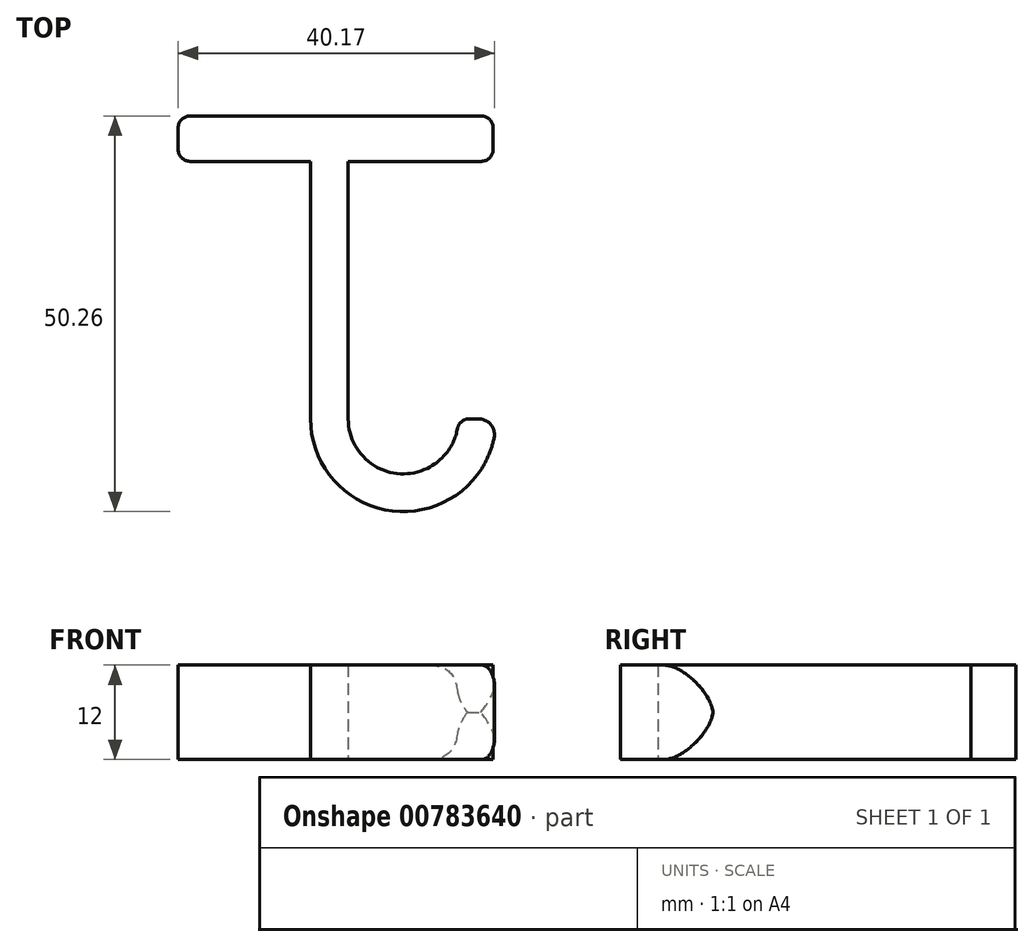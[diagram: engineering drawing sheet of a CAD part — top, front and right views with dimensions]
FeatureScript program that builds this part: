
annotation { "Feature Type Name" : "Feature", "Feature Type Description" : "" }
export const myFeature = defineFeature(function(context is Context, id is Id, definition is map)
    precondition{}
    {
        {
            var Q0;
            Q0=qCreatedBy(makeId("Top.planeOp"),FACE);
            var sketch = newSketch(context, id + "F0", { "sketchPlane" : qUnion([Q0])});
            skLineSegment(sketch, "E0.bottom", {"start": v(-44.99, 50) * mm, "end": v(-7.99, 50) * mm});
            skLineSegment(sketch, "E0.top", {"start": v(-44.99, 44.24) * mm, "end": v(-29.68, 44.24) * mm});
            skLineSegment(sketch, "E0.left", {"start": v(-46.49, 48.5) * mm, "end": v(-46.49, 45.74) * mm});
            skLineSegment(sketch, "E0.right", {"start": v(-6.49, 48.5) * mm, "end": v(-6.49, 45.74) * mm});
            skLineSegment(sketch, "E1.bottom", {"start": v(-29.68, 11.52) * mm, "end": v(-24.89, 11.52) * mm});
            skLineSegment(sketch, "E1.top", {"start": v(-29.68, 82.72) * mm, "end": v(-24.89, 82.72) * mm});
            skLineSegment(sketch, "E1.left", {"start": v(-29.68, 11.52) * mm, "end": v(-29.68, 50) * mm});
            skLineSegment(sketch, "E1.right", {"start": v(-24.89, 11.52) * mm, "end": v(-24.89, 44.24) * mm});
            skArc(sketch, "E2", {"start": v(-29.68, 11.52) * mm, "mid": v(-19.1, -0.2) * mm, "end": v(-6.36, 9.11) * mm});
            skArc(sketch, "E3", {"start": v(-24.89, 11.52) * mm, "mid": v(-18.52, 4.56) * mm, "end": v(-11.02, 10.28) * mm});
            skLineSegment(sketch, "E4", {"start": v(-8.32, 11.52) * mm, "end": v(-9.54, 11.52) * mm});
            skPoint(sketch, "E5", {"position": v(-24.89, 44.24) * mm});
            skPoint(sketch, "E6", {"position": v(-29.68, 44.24) * mm});
            skLineSegment(sketch, "E7", {"start": v(-24.89, 44.24) * mm, "end": v(-24.89, 50) * mm});
            skLineSegment(sketch, "E8", {"start": v(-29.68, 44.24) * mm, "end": v(-24.89, 44.24) * mm});
            skLineSegment(sketch, "E9", {"start": v(-24.89, 44.24) * mm, "end": v(-24.89, 44.24) * mm});
            skLineSegment(sketch, "E10", {"start": v(-24.89, 44.24) * mm, "end": v(-7.99, 44.24) * mm});
            skPoint(sketch, "E11.visualSharp", {"position": v(-46.49, 50) * mm});
            skArc(sketch, "E11.filletArc", {"start": v(-44.99, 50) * mm, "mid": v(-46.05, 49.56) * mm, "end": v(-46.49, 48.5) * mm});
            skPoint(sketch, "E12.visualSharp", {"position": v(-46.49, 44.24) * mm});
            skArc(sketch, "E12.filletArc", {"start": v(-46.49, 45.74) * mm, "mid": v(-46.05, 44.68) * mm, "end": v(-44.99, 44.24) * mm});
            skPoint(sketch, "E13.visualSharp", {"position": v(-6.49, 44.24) * mm});
            skArc(sketch, "E13.filletArc", {"start": v(-7.99, 44.24) * mm, "mid": v(-6.93, 44.68) * mm, "end": v(-6.49, 45.74) * mm});
            skPoint(sketch, "E14.visualSharp", {"position": v(-6.49, 50) * mm});
            skArc(sketch, "E14.filletArc", {"start": v(-6.49, 48.5) * mm, "mid": v(-6.93, 49.56) * mm, "end": v(-7.99, 50) * mm});
            skArc(sketch, "E15.filletArc", {"start": v(-9.54, 11.52) * mm, "mid": v(-10.5, 11.17) * mm, "end": v(-11.02, 10.28) * mm});
            skArc(sketch, "E16.filletArc", {"start": v(-6.36, 9.11) * mm, "mid": v(-6.77, 10.78) * mm, "end": v(-8.32, 11.52) * mm});
            skSolve(sketch);
        }
        {
            var Q0;
            Q0 = qSketchRegion(id + "F0", true);
            extrude(context, id + "F1", {"entities" : qUnion([Q0]), "depth" : 12 * mm, "offsetDistance" : 25 * mm});
        }
        {
            var Q0;
            Q0=makeQuery(id+"F1.opExtrude","CAP_EDGE",EDGE,{"disambiguationData":[OSD([sQuery(id+"F0.wireOp",EDGE,"E16.filletArc")])],"isStart":true});
            var Q1;
            Q1=makeQuery(id+"F1.opExtrude","CAP_EDGE",EDGE,{"disambiguationData":[OSD([sQuery(id+"F0.wireOp",EDGE,"E4")])],"isStart":true});
            var Q2;
            Q2=makeQuery(id+"F1.opExtrude","CAP_EDGE",EDGE,{"disambiguationData":[OSD([sQuery(id+"F0.wireOp",EDGE,"E15.filletArc")])],"isStart":true});
            var Q3;
            Q3=makeQuery(id+"F1.opExtrude","CAP_EDGE",EDGE,{"disambiguationData":[OSD([sQuery(id+"F0.wireOp",EDGE,"E4")])],"isStart":false});
            var Q4;
            Q4=makeQuery(id+"F1.opExtrude","CAP_EDGE",EDGE,{"disambiguationData":[OSD([sQuery(id+"F0.wireOp",EDGE,"E15.filletArc")])],"isStart":false});
            var Q5;
            Q5=makeQuery(id+"F1.opExtrude","CAP_EDGE",EDGE,{"disambiguationData":[OSD([sQuery(id+"F0.wireOp",EDGE,"E16.filletArc")])],"isStart":false});
            fillet(context, id + "F2", {"entities" : qUnion([Q0, Q1, Q2, Q3, Q4, Q5]), "radius" : 6.28 * mm, "rho" : 0.3, "crossSection" : FilletCrossSection.CONIC, "allowEdgeOverflow" : false});
        }
    });
